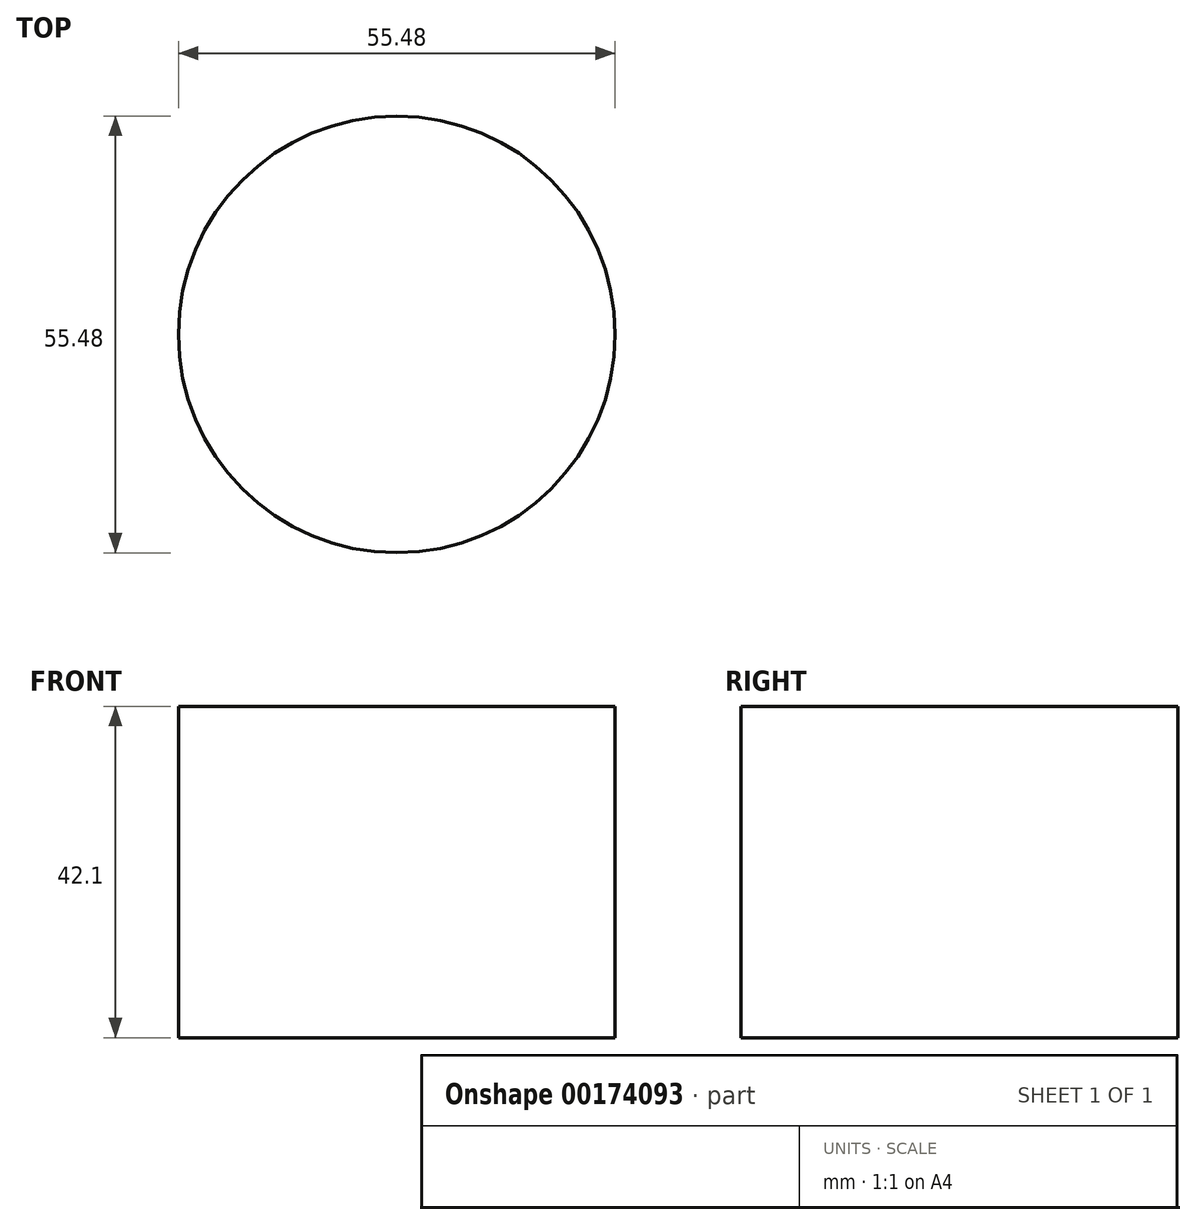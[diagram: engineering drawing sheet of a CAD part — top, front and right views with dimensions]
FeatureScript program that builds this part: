
annotation { "Feature Type Name" : "Feature", "Feature Type Description" : "" }
export const myFeature = defineFeature(function(context is Context, id is Id, definition is map)
    precondition{}
    {
        {
            var Q0;
            Q0=qCreatedBy(makeId("Front.planeOp"),FACE);
            var sketch = newSketch(context, id + "F0", { "sketchPlane" : qUnion([Q0])});
            skLineSegment(sketch, "E0.bottom", {"start": v(0, 42.1) * mm, "end": v(27.74, 42.1) * mm});
            skLineSegment(sketch, "E0.top", {"start": v(0, 0) * mm, "end": v(27.74, 0) * mm});
            skLineSegment(sketch, "E0.left", {"start": v(0, 42.1) * mm, "end": v(0, 0) * mm});
            skLineSegment(sketch, "E0.right", {"start": v(27.74, 42.1) * mm, "end": v(27.74, 0) * mm});
            skLineSegment(sketch, "E1.bottom", {"start": v(0, 0) * mm, "end": v(15.85, 0) * mm});
            skLineSegment(sketch, "E1.top", {"start": v(0, -35.17) * mm, "end": v(15.85, -35.17) * mm});
            skLineSegment(sketch, "E1.left", {"start": v(0, 0) * mm, "end": v(0, -35.17) * mm});
            skLineSegment(sketch, "E1.right", {"start": v(15.85, 0) * mm, "end": v(15.85, -35.17) * mm});
            skSolve(sketch);
        }
        {
            var Q0;
            Q0=makeQuery(id+"F0.imprint","IMPRINT",FACE,{"disambiguationData":[TD([[makeQuery(id+"F0.imprint","IMPRINT",EDGE,{"derivedFrom":sQuery(id+"F0.wireOp",EDGE,"E0.bottom")}),-1.0]])]});
            var Q1;
            Q1=makeQuery(id+"F0.imprint","IMPRINT",FACE,{"disambiguationData":[TD([[makeQuery(id+"F0.imprint","IMPRINT",EDGE,{"derivedFrom":sQuery(id+"F0.wireOp",EDGE,"E1.bottom")}),-1.0]])]});
            var Q2;
            Q2=sQuery(id+"F0.wireOp",EDGE,"E0.left");
            revolve(context, id + "F1", {"entities" : qUnion([Q0, Q1]), "axis" : qUnion([Q2]), "revolveType" : RevolveType.FULL});
        }
    });
